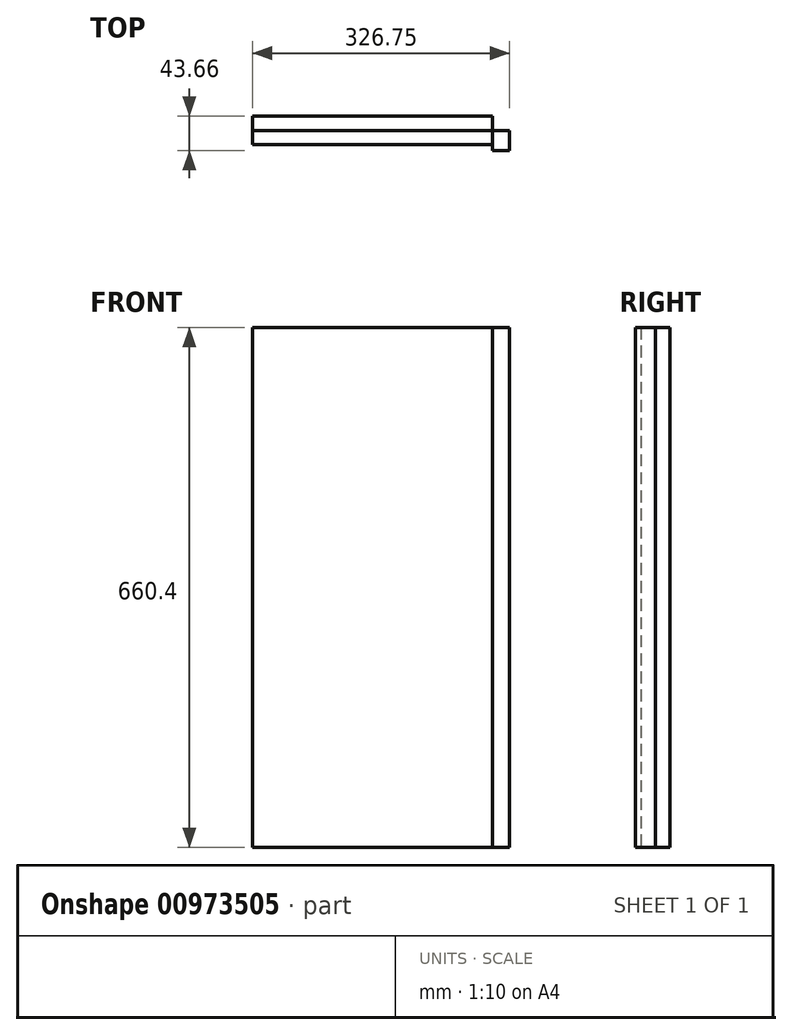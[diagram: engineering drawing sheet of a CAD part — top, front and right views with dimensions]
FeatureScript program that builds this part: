
annotation { "Feature Type Name" : "Feature", "Feature Type Description" : "" }
export const myFeature = defineFeature(function(context is Context, id is Id, definition is map)
    precondition{}
    {
        {
            var Q0;
            Q0=qCreatedBy(makeId("Front.planeOp"),FACE);
            var sketch = newSketch(context, id + "F0", { "sketchPlane" : qUnion([Q0])});
            skLineSegment(sketch, "E0.bottom", {"start": v(-152.4, 330.2) * mm, "end": v(152.4, 330.2) * mm});
            skLineSegment(sketch, "E0.top", {"start": v(-152.4, -330.2) * mm, "end": v(152.4, -330.2) * mm});
            skLineSegment(sketch, "E0.left", {"start": v(-152.4, 330.2) * mm, "end": v(-152.4, -330.2) * mm});
            skLineSegment(sketch, "E0.right", {"start": v(152.4, 330.2) * mm, "end": v(152.4, -330.2) * mm});
            skPoint(sketch, "E0.middle", {"position": v(0, 0) * mm});
            skSolve(sketch);
        }
        {
            var Q0;
            Q0 = qSketchRegion(id + "F0", true);
            extrude(context, id + "F1", {"entities" : qUnion([Q0]), "depth" : 18.26 * mm, "offsetDistance" : 25.4 * mm});
        }
        {
            var Q0;
            Q0=makeQuery(id+"F1.opExtrude","CAP_FACE",FACE,{"disambiguationData":[OSD([sQuery(id+"F0.wireOp",EDGE,"E0.bottom"),sQuery(id+"F0.wireOp",EDGE,"E0.top"),sQuery(id+"F0.wireOp",EDGE,"E0.left"),sQuery(id+"F0.wireOp",EDGE,"E0.right")])],"isStart":false});
            var sketch = newSketch(context, id + "F2", { "sketchPlane" : qUnion([Q0])});
            skLineSegment(sketch, "E1.bottom", {"start": v(152.4, 330.2) * mm, "end": v(174.35, 330.2) * mm});
            skLineSegment(sketch, "E1.top", {"start": v(152.4, -330.2) * mm, "end": v(174.35, -330.2) * mm});
            skLineSegment(sketch, "E1.left", {"start": v(152.4, 330.2) * mm, "end": v(152.4, -330.2) * mm});
            skLineSegment(sketch, "E1.right", {"start": v(174.35, 330.2) * mm, "end": v(174.35, -330.2) * mm});
            skSolve(sketch);
        }
        {
            var Q0;
            Q0=makeQuery(id+"F2.imprint","IMPRINT",FACE,{"disambiguationData":[TD([[makeQuery(id+"F2.imprint","IMPRINT",EDGE,{"derivedFrom":sQuery(id+"F2.wireOp",EDGE,"E1.bottom")}),-1.0]])]});
            extrude(context, id + "F3", {"entities" : qUnion([Q0]), "depth" : 25.4 * mm, "offsetDistance" : 25.4 * mm});
        }
        {
            var Q0;
            Q0=makeQuery(id+"F1.opExtrude","SWEPT_BODY",BODY,{"disambiguationData":[OSD([sQuery(id+"F0.wireOp",EDGE,"E0.bottom"),sQuery(id+"F0.wireOp",EDGE,"E0.top"),sQuery(id+"F0.wireOp",EDGE,"E0.left"),sQuery(id+"F0.wireOp",EDGE,"E0.right")])]});
            transform(context, id + "F4", {"entities" : qUnion([Q0]), "transformType" : TransformType.TRANSLATION_3D, "dx" : 0 * mm, "dy" : -18.26 * mm, "dz" : 0 * mm, "makeCopy" : true});
        }
    });
